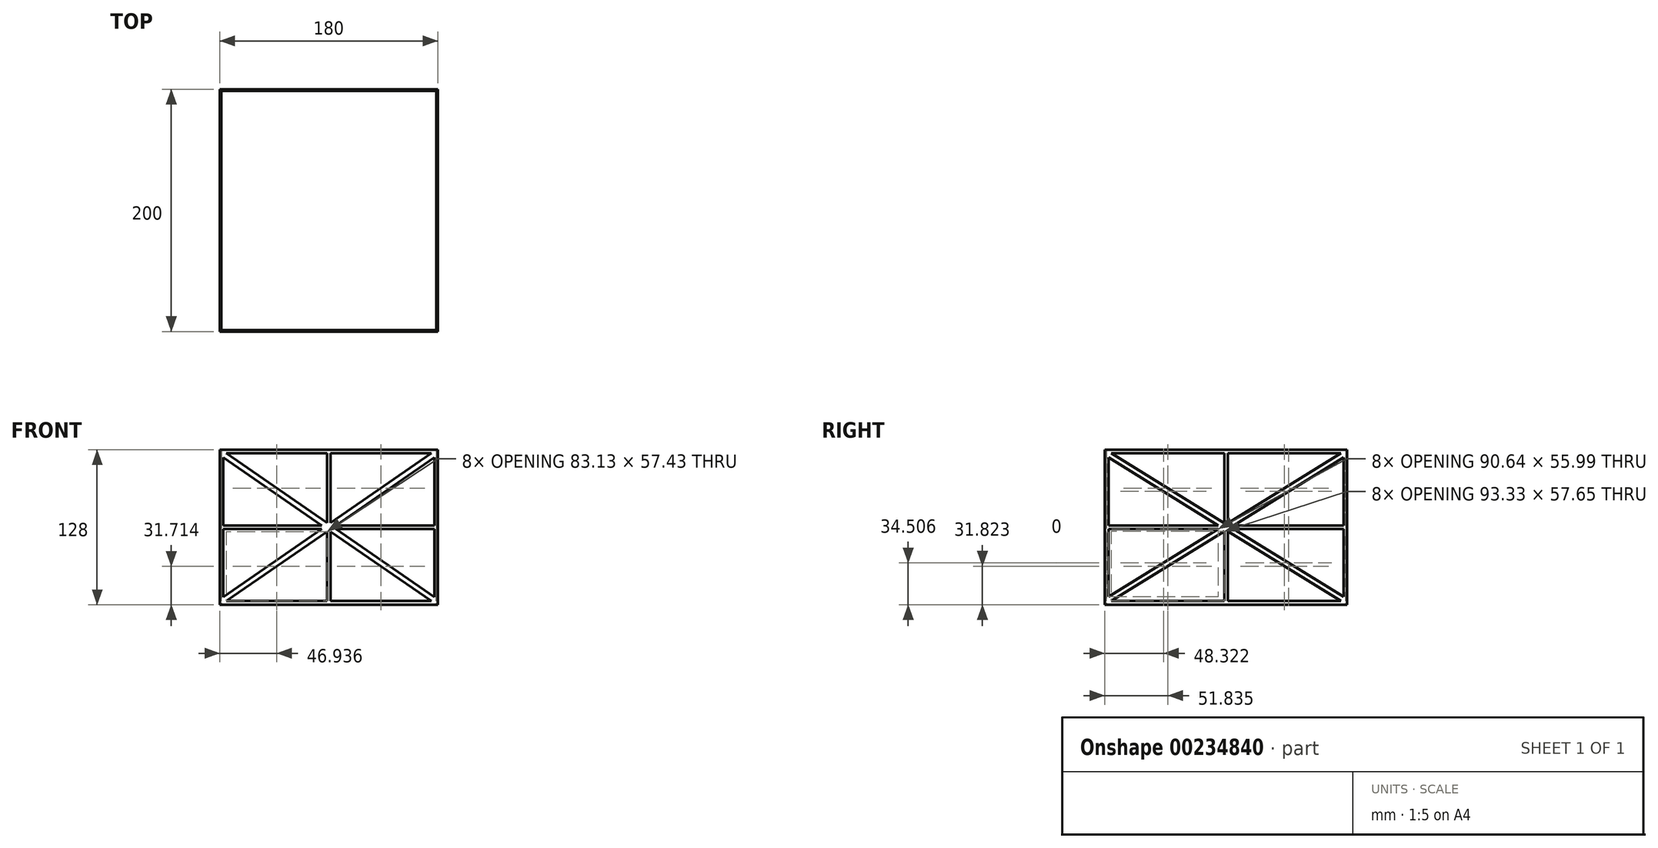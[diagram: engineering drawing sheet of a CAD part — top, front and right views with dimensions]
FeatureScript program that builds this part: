
annotation { "Feature Type Name" : "Feature", "Feature Type Description" : "" }
export const myFeature = defineFeature(function(context is Context, id is Id, definition is map)
    precondition{}
    {
        {
            var Q0;
            Q0=qCreatedBy(makeId("Top.planeOp"),FACE);
            var sketch = newSketch(context, id + "F0", { "sketchPlane" : qUnion([Q0])});
            skLineSegment(sketch, "E0.bottom", {"start": v(0, 0) * mm, "end": v(180, 0) * mm});
            skLineSegment(sketch, "E0.top", {"start": v(0, 200) * mm, "end": v(180, 200) * mm});
            skLineSegment(sketch, "E0.left", {"start": v(0, 0) * mm, "end": v(0, 200) * mm});
            skLineSegment(sketch, "E0.right", {"start": v(180, 0) * mm, "end": v(180, 200) * mm});
            skLineSegment(sketch, "E1.0", {"start": v(1.2, 198.8) * mm, "end": v(178.8, 198.8) * mm});
            skLineSegment(sketch, "E1.1", {"start": v(1.2, 1.2) * mm, "end": v(1.2, 198.8) * mm});
            skLineSegment(sketch, "E1.2", {"start": v(1.2, 1.2) * mm, "end": v(178.8, 1.2) * mm});
            skLineSegment(sketch, "E1.3", {"start": v(178.8, 1.2) * mm, "end": v(178.8, 198.8) * mm});
            skSolve(sketch);
        }
        {
            var Q0;
            Q0=makeQuery(id+"F0.imprint","IMPRINT",FACE,{"disambiguationData":[TD([[makeQuery(id+"F0.imprint","IMPRINT",EDGE,{"derivedFrom":sQuery(id+"F0.wireOp",EDGE,"E0.bottom")}),1.0]])]});
            extrude(context, id + "F1", {"entities" : qUnion([Q0]), "depth" : 128 * mm});
        }
        {
            var Q0;
            Q0=makeQuery(id+"F1.opExtrude","SWEPT_FACE",FACE,{"disambiguationData":[OSD([sQuery(id+"F0.wireOp",EDGE,"E0.bottom")])]});
            var sketch = newSketch(context, id + "F2", { "sketchPlane" : qUnion([Q0])});
            skLineSegment(sketch, "E2.0", {"start": v(3, 3) * mm, "end": v(177, 3) * mm});
            skLineSegment(sketch, "E2.1", {"start": v(3, 125) * mm, "end": v(3, 3) * mm});
            skLineSegment(sketch, "E2.2", {"start": v(177, 125) * mm, "end": v(3, 125) * mm});
            skLineSegment(sketch, "E2.3", {"start": v(177, 3) * mm, "end": v(177, 125) * mm});
            skLineSegment(sketch, "E3", {"start": v(90, 125) * mm, "end": v(90, 3) * mm, "construction": true});
            skLineSegment(sketch, "E4", {"start": v(3, 64) * mm, "end": v(177, 64) * mm, "construction": true});
            skLineSegment(sketch, "E5.0", {"start": v(3, 62.5) * mm, "end": v(177, 62.5) * mm});
            skLineSegment(sketch, "E6.0", {"start": v(3, 65.5) * mm, "end": v(177, 65.5) * mm});
            skLineSegment(sketch, "E7.0", {"start": v(88.5, 125) * mm, "end": v(88.5, 3) * mm});
            skLineSegment(sketch, "E8.0", {"start": v(91.5, 125) * mm, "end": v(91.5, 3) * mm});
            skLineSegment(sketch, "E9", {"start": v(3, 121.57) * mm, "end": v(174.63, 3) * mm});
            skLineSegment(sketch, "E10", {"start": v(5.37, 125) * mm, "end": v(177, 6.43) * mm});
            skLineSegment(sketch, "E11", {"start": v(174.63, 125) * mm, "end": v(3, 6.43) * mm});
            skLineSegment(sketch, "E12", {"start": v(177, 121.57) * mm, "end": v(5.37, 3) * mm});
            skPoint(sketch, "E13", {"position": v(91.5, 65.5) * mm});
            skPoint(sketch, "E14", {"position": v(88.5, 65.5) * mm});
            skPoint(sketch, "E15", {"position": v(88.5, 62.5) * mm});
            skPoint(sketch, "E16", {"position": v(91.5, 62.5) * mm});
            skLineSegment(sketch, "E17", {"start": v(3, 121.57) * mm, "end": v(5.37, 125) * mm, "construction": true});
            skLineSegment(sketch, "E18", {"start": v(3, 6.43) * mm, "end": v(5.37, 3) * mm, "construction": true});
            skSolve(sketch);
        }
        {
            var Q0;
            {var subQ0=sQuery(id+"F2.wireOp",EDGE,"E6.0");var subQ1=sQuery(id+"F2.wireOp",EDGE,"E2.1");var subQ2=makeQuery(id+"F2.imprint","INTERSECT",VERTEX,{"derivedFrom":[subQ1,subQ0]});Q0=makeQuery(id+"F2.imprint","IMPRINT",FACE,{"disambiguationData":[TD([[makeQuery(id+"F2.imprint","IMPRINT",EDGE,{"disambiguationData":[TD([[subQ2,1.0]])],"derivedFrom":subQ1}),1.0]])]});}
            var Q1;
            {var subQ0=sQuery(id+"F2.wireOp",EDGE,"E7.0");var subQ1=sQuery(id+"F2.wireOp",EDGE,"E2.2");var subQ2=makeQuery(id+"F2.imprint","INTERSECT",VERTEX,{"derivedFrom":[subQ1,subQ0]});Q1=makeQuery(id+"F2.imprint","IMPRINT",FACE,{"disambiguationData":[TD([[makeQuery(id+"F2.imprint","IMPRINT",EDGE,{"disambiguationData":[TD([[subQ2,-1.0]])],"derivedFrom":subQ1}),1.0]])]});}
            var Q2;
            {var subQ0=sQuery(id+"F2.wireOp",EDGE,"E8.0");var subQ1=sQuery(id+"F2.wireOp",EDGE,"E2.2");var subQ2=makeQuery(id+"F2.imprint","INTERSECT",VERTEX,{"derivedFrom":[subQ1,subQ0]});Q2=makeQuery(id+"F2.imprint","IMPRINT",FACE,{"disambiguationData":[TD([[makeQuery(id+"F2.imprint","IMPRINT",EDGE,{"disambiguationData":[TD([[subQ2,1.0]])],"derivedFrom":subQ1}),1.0]])]});}
            var Q3;
            {var subQ0=sQuery(id+"F2.wireOp",EDGE,"E6.0");var subQ1=sQuery(id+"F2.wireOp",EDGE,"E2.3");var subQ2=makeQuery(id+"F2.imprint","INTERSECT",VERTEX,{"derivedFrom":[subQ1,subQ0]});Q3=makeQuery(id+"F2.imprint","IMPRINT",FACE,{"disambiguationData":[TD([[makeQuery(id+"F2.imprint","IMPRINT",EDGE,{"disambiguationData":[TD([[subQ2,-1.0]])],"derivedFrom":subQ1}),1.0]])]});}
            var Q4;
            {var subQ0=sQuery(id+"F2.wireOp",EDGE,"E5.0");var subQ1=sQuery(id+"F2.wireOp",EDGE,"E2.3");var subQ2=makeQuery(id+"F2.imprint","INTERSECT",VERTEX,{"derivedFrom":[subQ1,subQ0]});Q4=makeQuery(id+"F2.imprint","IMPRINT",FACE,{"disambiguationData":[TD([[makeQuery(id+"F2.imprint","IMPRINT",EDGE,{"disambiguationData":[TD([[subQ2,1.0]])],"derivedFrom":subQ1}),1.0]])]});}
            var Q5;
            {var subQ0=sQuery(id+"F2.wireOp",EDGE,"E8.0");var subQ1=sQuery(id+"F2.wireOp",EDGE,"E2.0");var subQ2=makeQuery(id+"F2.imprint","INTERSECT",VERTEX,{"derivedFrom":[subQ1,subQ0]});Q5=makeQuery(id+"F2.imprint","IMPRINT",FACE,{"disambiguationData":[TD([[makeQuery(id+"F2.imprint","IMPRINT",EDGE,{"disambiguationData":[TD([[subQ2,-1.0]])],"derivedFrom":subQ1}),1.0]])]});}
            var Q6;
            {var subQ0=sQuery(id+"F2.wireOp",EDGE,"E7.0");var subQ1=sQuery(id+"F2.wireOp",EDGE,"E2.0");var subQ2=makeQuery(id+"F2.imprint","INTERSECT",VERTEX,{"derivedFrom":[subQ1,subQ0]});Q6=makeQuery(id+"F2.imprint","IMPRINT",FACE,{"disambiguationData":[TD([[makeQuery(id+"F2.imprint","IMPRINT",EDGE,{"disambiguationData":[TD([[subQ2,1.0]])],"derivedFrom":subQ1}),1.0]])]});}
            var Q7;
            {var subQ0=sQuery(id+"F2.wireOp",EDGE,"E5.0");var subQ1=sQuery(id+"F2.wireOp",EDGE,"E2.1");var subQ2=makeQuery(id+"F2.imprint","INTERSECT",VERTEX,{"derivedFrom":[subQ1,subQ0]});Q7=makeQuery(id+"F2.imprint","IMPRINT",FACE,{"disambiguationData":[TD([[makeQuery(id+"F2.imprint","IMPRINT",EDGE,{"disambiguationData":[TD([[subQ2,-1.0]])],"derivedFrom":subQ1}),1.0]])]});}
            extrude(context, id + "F3", {"entities" : qUnion([Q0, Q1, Q2, Q3, Q4, Q5, Q6, Q7]), "operationType" : NewBodyOperationType.REMOVE, "endBound" : BoundingType.THROUGH_ALL, "oppositeDirection" : true, "depth" : 25 * mm});
        }
        {
            var Q0;
            Q0=makeQuery(id+"F1.opExtrude","SWEPT_FACE",FACE,{"disambiguationData":[OSD([sQuery(id+"F0.wireOp",EDGE,"E0.right")])]});
            var sketch = newSketch(context, id + "F4", { "sketchPlane" : qUnion([Q0])});
            skLineSegment(sketch, "E19.0", {"start": v(3, 3) * mm, "end": v(197, 3) * mm});
            skLineSegment(sketch, "E19.1", {"start": v(3, 125) * mm, "end": v(3, 3) * mm});
            skLineSegment(sketch, "E19.2", {"start": v(197, 125) * mm, "end": v(3, 125) * mm});
            skLineSegment(sketch, "E19.3", {"start": v(197, 3) * mm, "end": v(197, 125) * mm});
            skLineSegment(sketch, "E20", {"start": v(100, 125) * mm, "end": v(100, 3) * mm, "construction": true});
            skLineSegment(sketch, "E21", {"start": v(3, 64) * mm, "end": v(197, 64) * mm, "construction": true});
            skLineSegment(sketch, "E22.0", {"start": v(3, 62.5) * mm, "end": v(197, 62.5) * mm});
            skLineSegment(sketch, "E23.0", {"start": v(3, 65.5) * mm, "end": v(197, 65.5) * mm});
            skLineSegment(sketch, "E24.0", {"start": v(98.5, 125) * mm, "end": v(98.5, 3) * mm});
            skLineSegment(sketch, "E25.0", {"start": v(101.5, 125) * mm, "end": v(101.5, 3) * mm});
            skPoint(sketch, "E26", {"position": v(98.5, 65.5) * mm});
            skPoint(sketch, "E27", {"position": v(101.5, 65.5) * mm});
            skPoint(sketch, "E28", {"position": v(101.5, 62.5) * mm});
            skPoint(sketch, "E29", {"position": v(98.5, 62.5) * mm});
            skLineSegment(sketch, "E30", {"start": v(3, 121.49) * mm, "end": v(194.83, 3) * mm});
            skLineSegment(sketch, "E31", {"start": v(197, 6.51) * mm, "end": v(5.17, 125) * mm});
            skLineSegment(sketch, "E32", {"start": v(3, 6.51) * mm, "end": v(194.83, 125) * mm});
            skLineSegment(sketch, "E33", {"start": v(5.17, 3) * mm, "end": v(197, 121.49) * mm});
            skLineSegment(sketch, "E34", {"start": v(5.17, 125) * mm, "end": v(3, 121.49) * mm, "construction": true});
            skLineSegment(sketch, "E35", {"start": v(3, 6.51) * mm, "end": v(5.17, 3) * mm, "construction": true});
            skSolve(sketch);
        }
        {
            var Q0;
            {var subQ0=sQuery(id+"F4.wireOp",EDGE,"E23.0");var subQ1=sQuery(id+"F4.wireOp",EDGE,"E19.1");var subQ2=makeQuery(id+"F4.imprint","INTERSECT",VERTEX,{"derivedFrom":[subQ1,subQ0]});Q0=makeQuery(id+"F4.imprint","IMPRINT",FACE,{"disambiguationData":[TD([[makeQuery(id+"F4.imprint","IMPRINT",EDGE,{"disambiguationData":[TD([[subQ2,1.0]])],"derivedFrom":subQ1}),1.0]])]});}
            var Q1;
            {var subQ0=sQuery(id+"F4.wireOp",EDGE,"E24.0");var subQ1=sQuery(id+"F4.wireOp",EDGE,"E19.2");var subQ2=makeQuery(id+"F4.imprint","INTERSECT",VERTEX,{"derivedFrom":[subQ1,subQ0]});Q1=makeQuery(id+"F4.imprint","IMPRINT",FACE,{"disambiguationData":[TD([[makeQuery(id+"F4.imprint","IMPRINT",EDGE,{"disambiguationData":[TD([[subQ2,-1.0]])],"derivedFrom":subQ1}),1.0]])]});}
            var Q2;
            {var subQ0=sQuery(id+"F4.wireOp",EDGE,"E25.0");var subQ1=sQuery(id+"F4.wireOp",EDGE,"E19.2");var subQ2=makeQuery(id+"F4.imprint","INTERSECT",VERTEX,{"derivedFrom":[subQ1,subQ0]});Q2=makeQuery(id+"F4.imprint","IMPRINT",FACE,{"disambiguationData":[TD([[makeQuery(id+"F4.imprint","IMPRINT",EDGE,{"disambiguationData":[TD([[subQ2,1.0]])],"derivedFrom":subQ1}),1.0]])]});}
            var Q3;
            {var subQ0=sQuery(id+"F4.wireOp",EDGE,"E23.0");var subQ1=sQuery(id+"F4.wireOp",EDGE,"E19.3");var subQ2=makeQuery(id+"F4.imprint","INTERSECT",VERTEX,{"derivedFrom":[subQ1,subQ0]});Q3=makeQuery(id+"F4.imprint","IMPRINT",FACE,{"disambiguationData":[TD([[makeQuery(id+"F4.imprint","IMPRINT",EDGE,{"disambiguationData":[TD([[subQ2,-1.0]])],"derivedFrom":subQ1}),1.0]])]});}
            var Q4;
            {var subQ0=sQuery(id+"F4.wireOp",EDGE,"E22.0");var subQ1=sQuery(id+"F4.wireOp",EDGE,"E19.3");var subQ2=makeQuery(id+"F4.imprint","INTERSECT",VERTEX,{"derivedFrom":[subQ1,subQ0]});Q4=makeQuery(id+"F4.imprint","IMPRINT",FACE,{"disambiguationData":[TD([[makeQuery(id+"F4.imprint","IMPRINT",EDGE,{"disambiguationData":[TD([[subQ2,1.0]])],"derivedFrom":subQ1}),1.0]])]});}
            var Q5;
            {var subQ0=sQuery(id+"F4.wireOp",EDGE,"E25.0");var subQ1=sQuery(id+"F4.wireOp",EDGE,"E19.0");var subQ2=makeQuery(id+"F4.imprint","INTERSECT",VERTEX,{"derivedFrom":[subQ1,subQ0]});Q5=makeQuery(id+"F4.imprint","IMPRINT",FACE,{"disambiguationData":[TD([[makeQuery(id+"F4.imprint","IMPRINT",EDGE,{"disambiguationData":[TD([[subQ2,-1.0]])],"derivedFrom":subQ1}),1.0]])]});}
            var Q6;
            {var subQ0=sQuery(id+"F4.wireOp",EDGE,"E24.0");var subQ1=sQuery(id+"F4.wireOp",EDGE,"E19.0");var subQ2=makeQuery(id+"F4.imprint","INTERSECT",VERTEX,{"derivedFrom":[subQ1,subQ0]});Q6=makeQuery(id+"F4.imprint","IMPRINT",FACE,{"disambiguationData":[TD([[makeQuery(id+"F4.imprint","IMPRINT",EDGE,{"disambiguationData":[TD([[subQ2,1.0]])],"derivedFrom":subQ1}),1.0]])]});}
            var Q7;
            {var subQ0=sQuery(id+"F4.wireOp",EDGE,"E22.0");var subQ1=sQuery(id+"F4.wireOp",EDGE,"E19.1");var subQ2=makeQuery(id+"F4.imprint","INTERSECT",VERTEX,{"derivedFrom":[subQ1,subQ0]});Q7=makeQuery(id+"F4.imprint","IMPRINT",FACE,{"disambiguationData":[TD([[makeQuery(id+"F4.imprint","IMPRINT",EDGE,{"disambiguationData":[TD([[subQ2,-1.0]])],"derivedFrom":subQ1}),1.0]])]});}
            extrude(context, id + "F5", {"entities" : qUnion([Q0, Q1, Q2, Q3, Q4, Q5, Q6, Q7]), "operationType" : NewBodyOperationType.REMOVE, "endBound" : BoundingType.THROUGH_ALL, "oppositeDirection" : true, "depth" : 25 * mm});
        }
    });
